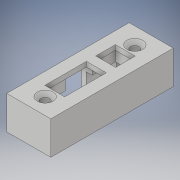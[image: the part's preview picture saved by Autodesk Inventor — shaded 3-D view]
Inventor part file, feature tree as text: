
AUTODESK INVENTOR PART (.ipt)
format: ipt  version: 2019 (Build 230136000, 136)  size: 206,848 bytes
history: native  units: mm
features: extrude x6, sketch x6, chamfer x2
ambient origin geometry x8: Origin, YZ Plane, XZ Plane, XY Plane, X Axis, Y Axis, Z Axis, Center Point
bodies: Solide1 (feature_tree)
feature tree (14):
  extrude  "Extrusion1"  Depth=50.0mm
  extrude  "Extrusion2"  Depth=18.0mm
  extrude  "Extrusion3"  Depth=13.6mm TaperAngle=0.0deg
  extrude  "Extrusion4"  Depth=28.8mm
  extrude  "Extrusion5"  Depth=8.1mm
  extrude  "Extrusion6"  Depth=13.6mm TaperAngle=0.0deg
  chamfer  "Chanfrein1"  Distance=32.7mm
  chamfer  "Chanfrein2"  Distance=3.5mm
  sketch  "Esquisse1"
  sketch  "Esquisse2"
  sketch  "Esquisse3"
  sketch  "Esquisse4"
  sketch  "Esquisse5"
  sketch  "Esquisse6"
